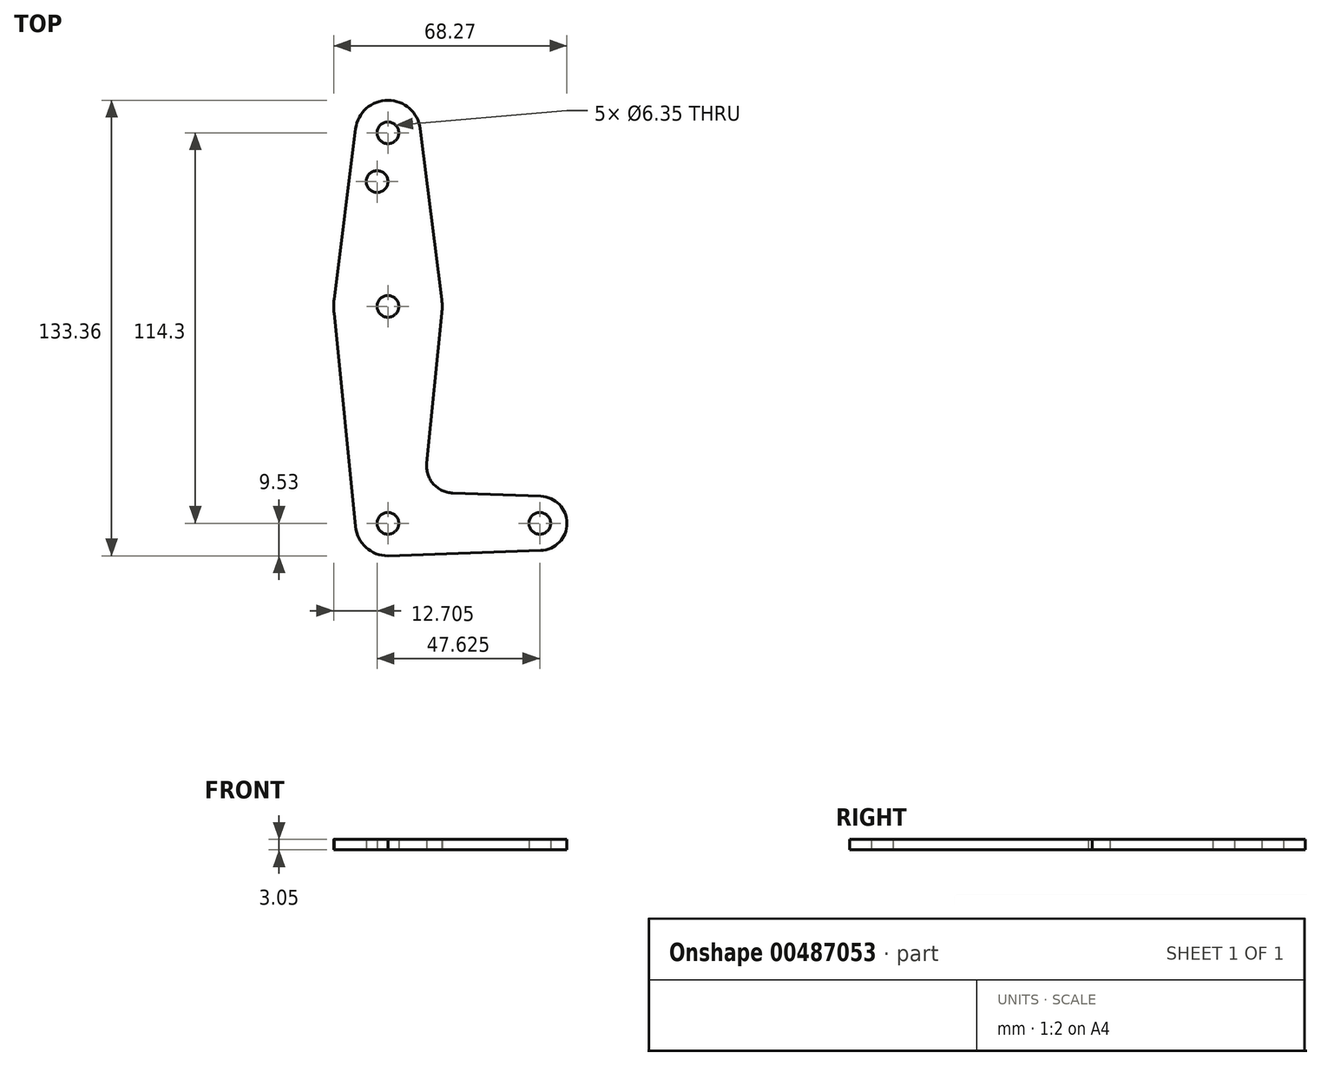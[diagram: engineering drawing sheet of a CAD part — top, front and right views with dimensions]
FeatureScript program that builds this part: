
annotation { "Feature Type Name" : "Feature", "Feature Type Description" : "" }
export const myFeature = defineFeature(function(context is Context, id is Id, definition is map)
    precondition{}
    {
        {
            var Q0;
            Q0=qCreatedBy(makeId("Top.planeOp"),FACE);
            var sketch = newSketch(context, id + "F0", { "sketchPlane" : qUnion([Q0])});
            skLineSegment(sketch, "E0", {"start": v(0, 0) * mm, "end": v(0, 114.3) * mm, "construction": true});
            skLineSegment(sketch, "E1", {"start": v(0, 0) * mm, "end": v(44.45, 0) * mm, "construction": true});
            skCircle(sketch, "E2", {"center": v(0, 0) * mm, "radius": 9.52 * mm});
            skCircle(sketch, "E3", {"center": v(0, 114.3) * mm, "radius": 9.53 * mm});
            skCircle(sketch, "E4", {"center": v(44.45, 0) * mm, "radius": 7.94 * mm});
            skCircle(sketch, "E5", {"center": v(0, 63.5) * mm, "radius": 15.88 * mm});
            skLineSegment(sketch, "E6", {"start": v(9.45, 115.5) * mm, "end": v(15.75, 65.48) * mm});
            skLineSegment(sketch, "E7", {"start": v(-9.45, 115.5) * mm, "end": v(-15.75, 65.48) * mm});
            skLineSegment(sketch, "E8", {"start": v(-15.75, 61.52) * mm, "end": v(-9.48, -0.95) * mm});
            skLineSegment(sketch, "E9", {"start": v(15.75, 61.52) * mm, "end": v(11.34, 17.6) * mm});
            skLineSegment(sketch, "E10", {"start": v(18.97, 8.85) * mm, "end": v(44.73, 7.93) * mm});
            skLineSegment(sketch, "E11", {"start": v(0, -9.52) * mm, "end": v(44.73, -7.93) * mm});
            skCircle(sketch, "E12", {"center": v(0, 114.3) * mm, "radius": 3.18 * mm});
            skCircle(sketch, "E13", {"center": v(0, 63.5) * mm, "radius": 3.17 * mm});
            skCircle(sketch, "E14", {"center": v(0, 0) * mm, "radius": 3.18 * mm});
            skCircle(sketch, "E15", {"center": v(44.45, 0) * mm, "radius": 3.18 * mm});
            skCircle(sketch, "E16", {"center": v(-3.18, 100.03) * mm, "radius": 3.18 * mm});
            skArc(sketch, "E17.filletArc", {"start": v(11.34, 17.6) * mm, "mid": v(13.26, 11.57) * mm, "end": v(18.97, 8.85) * mm});
            skSolve(sketch);
        }
        {
            var Q0;
            {var subQ0=sQuery(id+"F0.wireOp",EDGE,"E6");Q0=makeQuery(id+"F0.imprint","IMPRINT",FACE,{"disambiguationData":[TD([[makeQuery(id+"F0.imprint","IMPRINT",EDGE,{"derivedFrom":subQ0}),-1.0]])]});}
            var Q1;
            {var subQ0=sQuery(id+"F0.wireOp",EDGE,"E8");Q1=makeQuery(id+"F0.imprint","IMPRINT",FACE,{"disambiguationData":[TD([[makeQuery(id+"F0.imprint","IMPRINT",EDGE,{"derivedFrom":subQ0}),1.0]])]});}
            var Q2;
            Q2=makeQuery(id+"F0.imprint","IMPRINT",FACE,{"disambiguationData":[TD([[makeQuery(id+"F0.imprint","IMPRINT",EDGE,{"derivedFrom":sQuery(id+"F0.wireOp",EDGE,"E14")}),-1.0]])]});
            var Q3;
            Q3=makeQuery(id+"F0.imprint","IMPRINT",FACE,{"disambiguationData":[TD([[makeQuery(id+"F0.imprint","IMPRINT",EDGE,{"derivedFrom":sQuery(id+"F0.wireOp",EDGE,"E15")}),-1.0]])]});
            var Q4;
            Q4=makeQuery(id+"F0.imprint","IMPRINT",FACE,{"disambiguationData":[TD([[makeQuery(id+"F0.imprint","IMPRINT",EDGE,{"derivedFrom":sQuery(id+"F0.wireOp",EDGE,"E13")}),-1.0]])]});
            var Q5;
            Q5=makeQuery(id+"F0.imprint","IMPRINT",FACE,{"disambiguationData":[TD([[makeQuery(id+"F0.imprint","IMPRINT",EDGE,{"derivedFrom":sQuery(id+"F0.wireOp",EDGE,"E12")}),-1.0]])]});
            extrude(context, id + "F1", {"entities" : qUnion([Q0, Q1, Q2, Q3, Q4, Q5]), "depth" : 3.05 * mm});
        }
    });
